FCSTD DOCUMENT  (FreeCAD 0.20R29603 (Git))
Label: five_wires
License: All rights reserved
LicenseURL: http://en.wikipedia.org/wiki/All_rights_reserved
objects: Part::Part2DObjectPython×11, App::FeaturePython×8, App::DocumentObjectGroup×6
note: 11 computed .brp shape members not serialized (recipe doc carries the construction recipe); baked Part::Feature solids carry a one-line shape summary decoded from their .brp

FEATURE [Part::Part2DObjectPython] Circle  label="Conductor_0"  # Draft 2D object (typed FeaturePython)
  Area = 28.2743
  FirstAngle = 0
  LastAngle = 0
  MakeFace = true
  Radius = 3
FEATURE [Part::Part2DObjectPython] Circle001  label="Conductor_1"  # Draft 2D object (typed FeaturePython)
  Area = 2.01062
  FirstAngle = 0
  LastAngle = 0
  MakeFace = true
  Radius = 0.8
FEATURE [Part::Part2DObjectPython] Circle002  label="Dielectric_1"  # Draft 2D object (typed FeaturePython)
  Area = 3.14159
  FirstAngle = 0
  LastAngle = 0
  MakeFace = true
  Radius = 1
FEATURE [Part::Part2DObjectPython] Circle003  label="Conductor_002"  # Draft 2D object (typed FeaturePython)
  Area = 0.785398
  FirstAngle = 0
  LastAngle = 0
  MakeFace = true
  Placement = pos=(2,-1e-16,0) rot=(0,0,1;0rad)
  Radius = 0.5
FEATURE [Part::Part2DObjectPython] Circle004  label="Dielectric_002"  # Draft 2D object (typed FeaturePython)
  Area = 1.76715
  FirstAngle = 0
  LastAngle = 0
  MakeFace = true
  Placement = pos=(2,-1e-16,0) rot=(0,0,1;0rad)
  Radius = 0.75
FEATURE [App::DocumentObjectGroup] Group001  label="solid_wire_002"
  Group = -> [Circle003,Circle004]
FEATURE [Part::Part2DObjectPython] Circle005  label="Conductor_003"  # Draft 2D object (typed FeaturePython)
  Area = 0.785398
  FirstAngle = 0
  LastAngle = 0
  MakeFace = true
  Placement = pos=(0,-2,0) rot=(0,0,1;0rad)
  Radius = 0.5
FEATURE [Part::Part2DObjectPython] Circle006  label="Dielectric_003"  # Draft 2D object (typed FeaturePython)
  Area = 2.01062
  FirstAngle = 0
  LastAngle = 0
  MakeFace = true
  Placement = pos=(0,-2,0) rot=(0,0,1;0rad)
  Radius = 0.8
FEATURE [App::DocumentObjectGroup] Group002  label="solid_wire_003"
  Group = -> [Circle005,Circle006]
FEATURE [Part::Part2DObjectPython] Circle007  label="Dielectric_004"  # Draft 2D object (typed FeaturePython)
  Area = 2.01062
  FirstAngle = 0
  LastAngle = 0
  MakeFace = true
  Placement = pos=(-2,-1e-16,0) rot=(0,0,1;0rad)
  Radius = 0.8
FEATURE [Part::Part2DObjectPython] Circle008  label="Conductor_004"  # Draft 2D object (typed FeaturePython)
  Area = 0.785398
  FirstAngle = 0
  LastAngle = 0
  MakeFace = true
  Placement = pos=(-2,-1e-16,0) rot=(0,0,1;0rad)
  Radius = 0.5
FEATURE [Part::Part2DObjectPython] Circle009  label="Dielectric_005"  # Draft 2D object (typed FeaturePython)
  Area = 2.01062
  FirstAngle = 0
  LastAngle = 0
  MakeFace = true
  Placement = pos=(0,2,0) rot=(0,0,1;0rad)
  Radius = 0.8
FEATURE [Part::Part2DObjectPython] Circle010  label="Conductor_005"  # Draft 2D object (typed FeaturePython)
  Area = 0.785398
  FirstAngle = 0
  LastAngle = 0
  MakeFace = true
  Placement = pos=(0,2,0) rot=(0,0,1;0rad)
  Radius = 0.5
FEATURE [App::FeaturePython] dLabel  # WARN: FeaturePython — macro-defined, semantics opaque (R4)
  CustomText = solid_wire_1
  LabelType = 0
  Placement = pos=(1.57151,1.23572,0) rot=(0,0,1;0rad)
  Points = (3) [(1.57151,1.23572,0),(1.07624,1.23572,0),(0,0,0)]
  StraightDirection = 0
  StraightDistance = -0.495278
  TargetPoint = (0,0,0)
  Text = solid_wire_1
FEATURE [App::FeaturePython] dLabel001  # WARN: FeaturePython — macro-defined, semantics opaque (R4)
  CustomText = solid_wire_5
  LabelType = 0
  Placement = pos=(1.35862,3,0) rot=(0,0,1;0rad)
  Points = (3) [(1.35862,3,0),(1,3,0),(0,2,0)]
  StraightDirection = 0
  StraightDistance = -0.358622
  TargetPoint = (0,2,0)
  Text = solid_wire_5
FEATURE [App::DocumentObjectGroup] Group004  label="solid_wire_005"
  Group = -> [Circle010,Circle009,dLabel001]
FEATURE [App::FeaturePython] Dimension  # Draft dimension (typed FeaturePython)
  Diameter = true
  Dimline = (3.19741,-2.12682,0)
  Direction = (0,0,0)
  Distance = 6
  End = (-0.8,-3,0)
  Normal = (0,0,1)
  Start = (-0.8,3,0)
FEATURE [App::FeaturePython] Dimension001  # Draft dimension (typed FeaturePython)
  Diameter = false
  Dimline = (-3.25,-0.5,0)
  Direction = (0,0,0)
  Distance = 1
  End = (-2,-0.5,0)
  Normal = (0,0,1)
  Start = (-2,0.5,0)
FEATURE [App::FeaturePython] Dimension002  # Draft dimension (typed FeaturePython)
  Diameter = true
  Dimline = (-1.25,0.75,0)
  Direction = (0,0,0)
  Distance = 1.6
  End = (-1.43431,0.565685,0)
  LinkedGeometry = -> [Circle007]
  Normal = (0,0,1)
  Start = (-2.56569,-0.565685,0)
  Support = -> Circle007
FEATURE [App::DocumentObjectGroup] Group003  label="solid_wire_004"
  Group = -> [Circle008,Circle007,Dimension001,Dimension002]
FEATURE [App::DocumentObjectGroup] Group005  label="Domain_0"
  Group = -> [Dimension,Circle]
FEATURE [App::FeaturePython] Dimension003  # Draft dimension (typed FeaturePython)
  Diameter = false
  Dimline = (0.482231,-1.07185,0)
  Direction = (0,0,0)
  Distance = 2
  End = (1,1e-16,0)
  Normal = (0,0,1)
  Start = (-1,-1e-16,0)
FEATURE [App::FeaturePython] Dimension004  # Draft dimension (typed FeaturePython)
  Diameter = false
  Dimline = (0.6,-0.6,0)
  Direction = (0,0,0)
  Distance = 1.6
  End = (0.8,0,0)
  Normal = (0,0,1)
  Start = (-0.8,0,0)
FEATURE [App::DocumentObjectGroup] Group  label="solid_wire_1"
  Group = -> [Circle001,Circle002,dLabel,Dimension003,Dimension004]
FEATURE [App::FeaturePython] Dimension005  # Draft dimension (typed FeaturePython)
  Diameter = false
  Dimline = (-0.6,1,0)
  Direction = (0,0,0)
  Distance = 2
  End = (0,0,0)
  Normal = (0,0,1)
  Start = (0,2,0)
